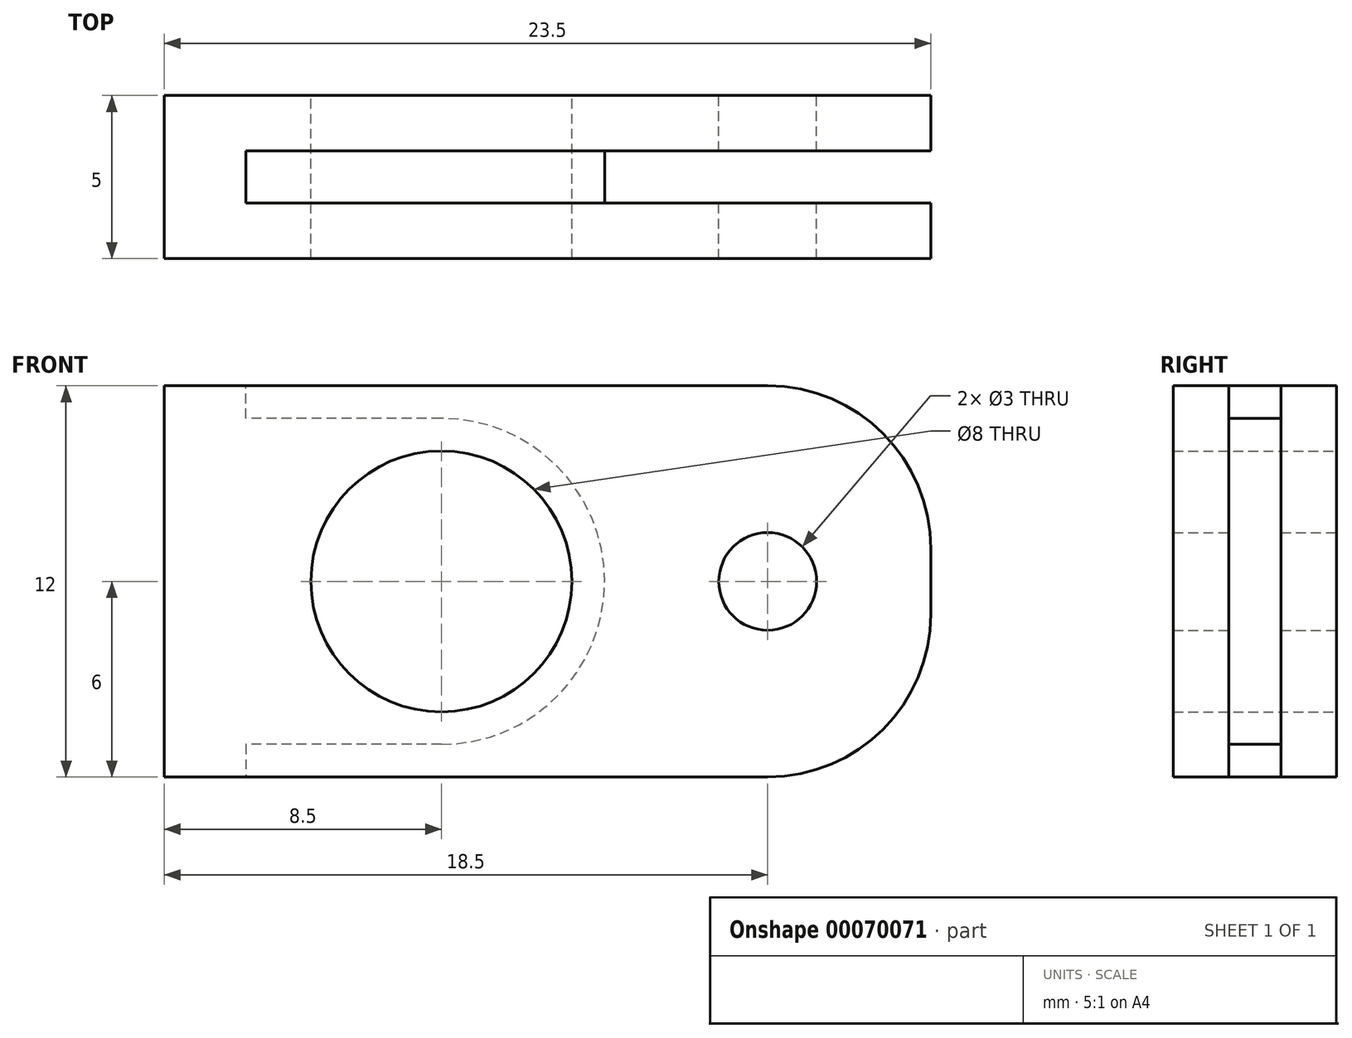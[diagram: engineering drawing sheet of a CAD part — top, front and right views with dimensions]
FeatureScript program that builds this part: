
annotation { "Feature Type Name" : "Feature", "Feature Type Description" : "" }
export const myFeature = defineFeature(function(context is Context, id is Id, definition is map)
    precondition{}
    {
        {
            var Q0;
            Q0=qCreatedBy(makeId("Front.planeOp"),FACE);
            var sketch = newSketch(context, id + "F0", { "sketchPlane" : qUnion([Q0])});
            skLineSegment(sketch, "E0.bottom", {"start": v(6, 6) * mm, "end": v(-6, 6) * mm});
            skLineSegment(sketch, "E0.top", {"start": v(6, -6) * mm, "end": v(-6, -6) * mm});
            skLineSegment(sketch, "E0.left", {"start": v(6, 6) * mm, "end": v(6, -6) * mm});
            skLineSegment(sketch, "E0.right", {"start": v(-6, 6) * mm, "end": v(-6, -6) * mm});
            skPoint(sketch, "E0.middle", {"position": v(0, 0) * mm});
            skCircle(sketch, "E1", {"center": v(0, 0) * mm, "radius": 4 * mm});
            skLineSegment(sketch, "E2", {"start": v(6, 0) * mm, "end": v(10, 0) * mm, "construction": true});
            skCircle(sketch, "E3", {"center": v(10, 0) * mm, "radius": 1.5 * mm});
            skLineSegment(sketch, "E4", {"start": v(10, 0) * mm, "end": v(15, 0) * mm, "construction": true});
            skLineSegment(sketch, "E5", {"start": v(6, 6) * mm, "end": v(10, 6) * mm});
            skLineSegment(sketch, "E6", {"start": v(15, 1) * mm, "end": v(15, 0) * mm});
            skLineSegment(sketch, "E7.MirrorCS", {"start": v(6, -6) * mm, "end": v(10, -6) * mm});
            skLineSegment(sketch, "E8.MirrorCS", {"start": v(15, -1) * mm, "end": v(15, 0) * mm});
            skPoint(sketch, "E9.visualSharp", {"position": v(15, 6) * mm});
            skArc(sketch, "E9.filletArc", {"start": v(15, 1) * mm, "mid": v(13.54, 4.54) * mm, "end": v(10, 6) * mm});
            skPoint(sketch, "E10.visualSharp", {"position": v(15, -6) * mm});
            skArc(sketch, "E10.filletArc", {"start": v(10, -6) * mm, "mid": v(13.54, -4.54) * mm, "end": v(15, -1) * mm});
            skLineSegment(sketch, "E11", {"start": v(-6, 0) * mm, "end": v(-8.5, 0) * mm, "construction": true});
            skPoint(sketch, "E11.endSnap0", {"position": v(-6, 0) * mm});
            skLineSegment(sketch, "E12", {"start": v(-8.5, 6) * mm, "end": v(-8.5, -6) * mm});
            skLineSegment(sketch, "E13", {"start": v(-8.5, 6) * mm, "end": v(-6, 6) * mm});
            skLineSegment(sketch, "E14", {"start": v(-8.5, -6) * mm, "end": v(-6, -6) * mm});
            skSolve(sketch);
        }
        {
            var Q0;
            Q0 = qSketchRegion(id + "F0", true);
            extrude(context, id + "F1", {"entities" : qUnion([Q0]), "endBound" : BoundingType.SYMMETRIC, "depth" : (1.6 + 3.4) * mm});
        }
        {
            var Q0;
            Q0=qCreatedBy(makeId("Front.planeOp"),FACE);
            var sketch = newSketch(context, id + "F2", { "sketchPlane" : qUnion([Q0])});
            skArc(sketch, "E15", {"start": v(0, 5) * mm, "mid": v(5, 0) * mm, "end": v(0, -5) * mm});
            skLineSegment(sketch, "E16.0", {"start": v(-6, 6) * mm, "end": v(-6, -6) * mm, "construction": true});
            skLineSegment(sketch, "E17.0", {"start": v(6, 6) * mm, "end": v(-6, 6) * mm});
            skLineSegment(sketch, "E18.0", {"start": v(6, -6) * mm, "end": v(-6, -6) * mm});
            skLineSegment(sketch, "E19.0", {"start": v(6, -6) * mm, "end": v(10, -6) * mm});
            skArc(sketch, "E20.0", {"start": v(10, -6) * mm, "mid": v(13.54, -4.54) * mm, "end": v(15, -1) * mm});
            skLineSegment(sketch, "E21.0", {"start": v(15, -1) * mm, "end": v(15, 0) * mm});
            skLineSegment(sketch, "E22.0", {"start": v(15, 1) * mm, "end": v(15, 0) * mm});
            skArc(sketch, "E23.0", {"start": v(15, 1) * mm, "mid": v(13.54, 4.54) * mm, "end": v(10, 6) * mm});
            skLineSegment(sketch, "E24.0", {"start": v(6, 6) * mm, "end": v(10, 6) * mm});
            skLineSegment(sketch, "E25.0", {"start": v(6, 6) * mm, "end": v(-6, 6) * mm, "construction": true});
            skLineSegment(sketch, "E26", {"start": v(0, 5) * mm, "end": v(-6, 5) * mm});
            skLineSegment(sketch, "E27", {"start": v(-6, 5) * mm, "end": v(-6, 6) * mm});
            skLineSegment(sketch, "E28.MirrorCS", {"start": v(0, -5) * mm, "end": v(-6, -5) * mm});
            skLineSegment(sketch, "E29.MirrorCS", {"start": v(-6, -5) * mm, "end": v(-6, -6) * mm});
            skSolve(sketch);
        }
        {
            var Q0;
            Q0 = qSketchRegion(id + "F2", true);
            var Q1;
            Q1 = qConstructionFilter(qBodyType(qCreatedBy(id + "F2" ,EDGE), BodyType.WIRE), ConstructionObject.NO);
            extrude(context, id + "F3", {"entities" : qUnion([Q0]), "operationType" : NewBodyOperationType.REMOVE, "surfaceEntities" : qUnion([Q1]), "endBound" : BoundingType.SYMMETRIC, "oppositeDirection" : true, "depth" : 1.6 * mm});
        }
    });
